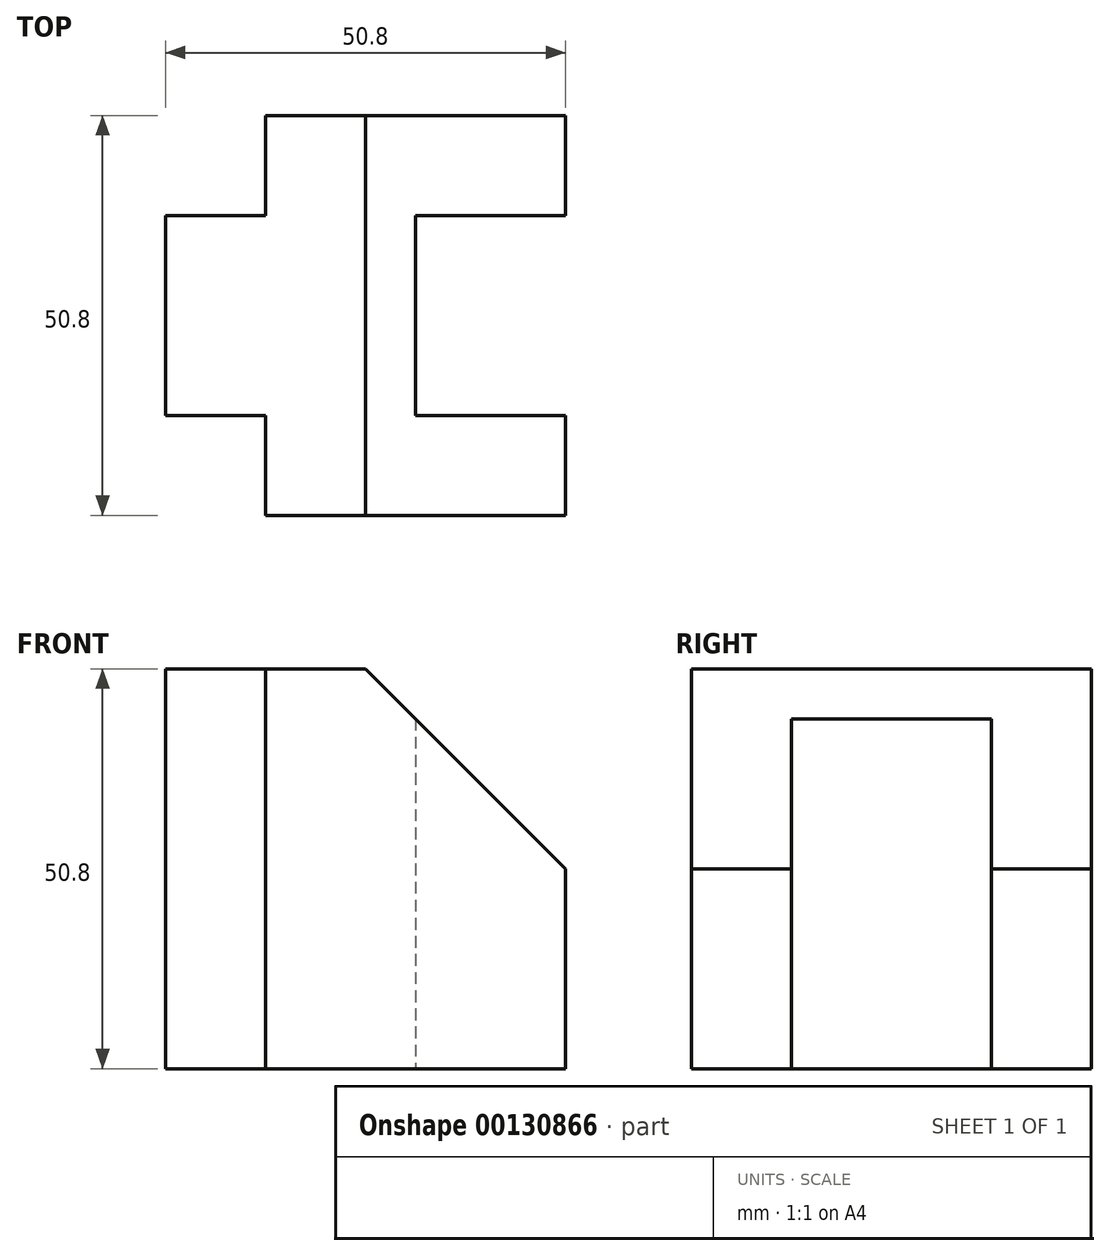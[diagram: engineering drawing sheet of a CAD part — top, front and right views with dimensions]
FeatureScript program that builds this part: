
annotation { "Feature Type Name" : "Feature", "Feature Type Description" : "" }
export const myFeature = defineFeature(function(context is Context, id is Id, definition is map)
    precondition{}
    {
        {
            var Q0;
            Q0=qCreatedBy(makeId("Top.planeOp"),FACE);
            var sketch = newSketch(context, id + "F0", { "sketchPlane" : qUnion([Q0])});
            skLineSegment(sketch, "E0", {"start": v(0, 0) * mm, "end": v(0, 12.7) * mm});
            skLineSegment(sketch, "E1", {"start": v(0, 12.7) * mm, "end": v(-12.7, 12.7) * mm});
            skLineSegment(sketch, "E2", {"start": v(-12.7, 12.7) * mm, "end": v(-12.7, 38.1) * mm});
            skLineSegment(sketch, "E3", {"start": v(-12.7, 38.1) * mm, "end": v(0, 38.1) * mm});
            skLineSegment(sketch, "E4", {"start": v(0, 38.1) * mm, "end": v(0, 50.8) * mm});
            skLineSegment(sketch, "E5", {"start": v(0, 50.8) * mm, "end": v(38.1, 50.8) * mm});
            skLineSegment(sketch, "E6", {"start": v(38.1, 50.8) * mm, "end": v(38.1, 38.1) * mm});
            skLineSegment(sketch, "E7", {"start": v(38.1, 38.1) * mm, "end": v(19.05, 38.1) * mm});
            skLineSegment(sketch, "E8", {"start": v(19.05, 38.1) * mm, "end": v(19.05, 12.7) * mm});
            skLineSegment(sketch, "E9", {"start": v(19.05, 12.7) * mm, "end": v(38.1, 12.7) * mm});
            skLineSegment(sketch, "E10", {"start": v(38.1, 12.7) * mm, "end": v(38.1, 0) * mm});
            skLineSegment(sketch, "E11", {"start": v(38.1, 0) * mm, "end": v(0, 0) * mm});
            skSolve(sketch);
        }
        {
            var Q0;
            Q0=makeQuery(id+"F0.imprint","IMPRINT",FACE,{"disambiguationData":[TD([[makeQuery(id+"F0.imprint","IMPRINT",EDGE,{"derivedFrom":sQuery(id+"F0.wireOp",EDGE,"E0")}),-1.0]])]});
            extrude(context, id + "F1", {"entities" : qUnion([Q0]), "depth" : 50.8 * mm});
        }
        {
            var Q0;
            Q0=makeQuery(id+"F1.opExtrude","SWEPT_FACE",FACE,{"disambiguationData":[OSD([sQuery(id+"F0.wireOp",EDGE,"E11")])]});
            var sketch = newSketch(context, id + "F2", { "sketchPlane" : qUnion([Q0])});
            skLineSegment(sketch, "E12", {"start": v(0, 50.8) * mm, "end": v(12.7, 50.8) * mm, "construction": true});
            skLineSegment(sketch, "E13", {"start": v(38.1, 0) * mm, "end": v(38.1, 25.4) * mm, "construction": true});
            skLineSegment(sketch, "E14", {"start": v(12.7, 50.8) * mm, "end": v(38.1, 50.8) * mm});
            skLineSegment(sketch, "E15", {"start": v(38.1, 50.8) * mm, "end": v(38.1, 25.4) * mm});
            skLineSegment(sketch, "E16", {"start": v(12.7, 50.8) * mm, "end": v(38.1, 25.4) * mm});
            skSolve(sketch);
        }
        {
            var Q0;
            Q0=makeQuery(id+"F2.imprint","IMPRINT",FACE,{"disambiguationData":[TD([[makeQuery(id+"F2.imprint","IMPRINT",EDGE,{"derivedFrom":sQuery(id+"F2.wireOp",EDGE,"E14")}),1.0]])]});
            extrude(context, id + "F3", {"entities" : qUnion([Q0]), "operationType" : NewBodyOperationType.REMOVE, "oppositeDirection" : true, "depth" : 50.8 * mm});
        }
    });
